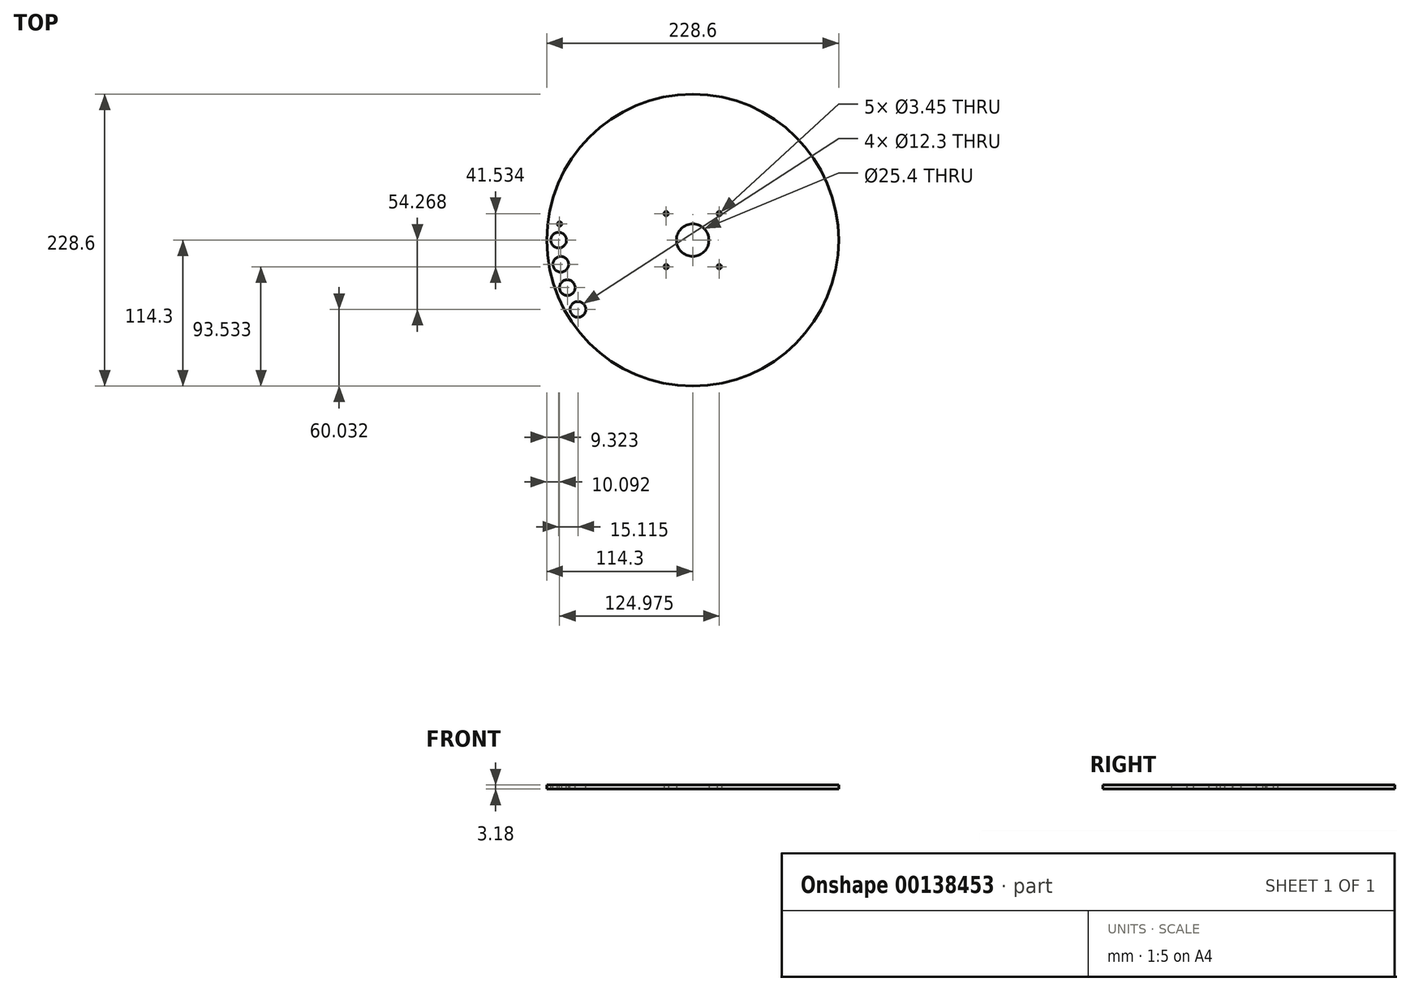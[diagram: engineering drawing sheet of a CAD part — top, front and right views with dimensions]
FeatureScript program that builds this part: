
annotation { "Feature Type Name" : "Feature", "Feature Type Description" : "" }
export const myFeature = defineFeature(function(context is Context, id is Id, definition is map)
    precondition{}
    {
        {
            var Q0;
            Q0=qCreatedBy(makeId("Top.planeOp"),FACE);
            var sketch = newSketch(context, id + "F0", { "sketchPlane" : qUnion([Q0])});
            skCircle(sketch, "E0", {"center": v(0, 0) * mm, "radius": 114.3 * mm});
            skCircle(sketch, "E1", {"center": v(0, 0) * mm, "radius": 12.7 * mm});
            skCircle(sketch, "E2", {"center": v(0, 0) * mm, "radius": 25.4 * mm, "construction": true});
            skLineSegment(sketch, "E3.bottom", {"start": v(-20.77, -20.77) * mm, "end": v(20.77, -20.77) * mm, "construction": true});
            skLineSegment(sketch, "E3.top", {"start": v(-20.77, 20.77) * mm, "end": v(20.77, 20.77) * mm, "construction": true});
            skLineSegment(sketch, "E3.left", {"start": v(-20.77, -20.77) * mm, "end": v(-20.77, 20.77) * mm, "construction": true});
            skLineSegment(sketch, "E3.right", {"start": v(20.77, -20.77) * mm, "end": v(20.77, 20.77) * mm, "construction": true});
            skCircle(sketch, "E4", {"center": v(-20.77, -20.77) * mm, "radius": 3.97 * mm, "construction": true});
            skCircle(sketch, "E5", {"center": v(-20.77, -20.77) * mm, "radius": 1.73 * mm});
            skCircle(sketch, "E6", {"center": v(-20.77, 20.77) * mm, "radius": 1.73 * mm});
            skCircle(sketch, "E7", {"center": v(20.77, 20.77) * mm, "radius": 1.73 * mm});
            skCircle(sketch, "E8", {"center": v(20.77, -20.77) * mm, "radius": 1.73 * mm});
            skSolve(sketch);
        }
        {
            var Q0;
            Q0 = qSketchRegion(id + "F0", true);
            extrude(context, id + "F1", {"entities" : qUnion([Q0]), "depth" : 3.17 * mm});
        }
        {
            var Q0;
            Q0=makeQuery(id+"F1.opExtrude","CAP_FACE",FACE,{"disambiguationData":[OSD([sQuery(id+"F0.wireOp",EDGE,"E0"),sQuery(id+"F0.wireOp",EDGE,"E1")])],"isStart":false});
            var sketch = newSketch(context, id + "F2", { "sketchPlane" : qUnion([Q0])});
            skLineSegment(sketch, "E9", {"start": v(0, 0) * mm, "end": v(-104.98, 0) * mm, "construction": true});
            skLineSegment(sketch, "E10", {"start": v(-104.98, 0) * mm, "end": v(-114.3, 0) * mm, "construction": true});
            skCircle(sketch, "E11", {"center": v(-104.98, 0) * mm, "radius": 6.15 * mm});
            skLineSegment(sketch, "E12", {"start": v(0, 0) * mm, "end": v(-103.26, -18.9) * mm, "construction": true});
            skLineSegment(sketch, "E13", {"start": v(0, 0) * mm, "end": v(-98.17, -37.2) * mm, "construction": true});
            skLineSegment(sketch, "E14", {"start": v(0, 0) * mm, "end": v(-89.86, -54.27) * mm, "construction": true});
            skLineSegment(sketch, "E15", {"start": v(0, 0) * mm, "end": v(-104.2, 12.68) * mm, "construction": true});
            skCircle(sketch, "E16", {"center": v(-103.26, -18.9) * mm, "radius": 6.15 * mm});
            skCircle(sketch, "E17", {"center": v(-98.17, -37.2) * mm, "radius": 6.15 * mm});
            skCircle(sketch, "E18", {"center": v(-89.86, -54.27) * mm, "radius": 6.15 * mm});
            skLineSegment(sketch, "E19", {"start": v(-104.98, 0) * mm, "end": v(-103.26, -18.9) * mm, "construction": true});
            skLineSegment(sketch, "E20", {"start": v(-98.17, -37.2) * mm, "end": v(-103.26, -18.9) * mm, "construction": true});
            skLineSegment(sketch, "E21", {"start": v(-98.17, -37.2) * mm, "end": v(-89.86, -54.27) * mm, "construction": true});
            skCircle(sketch, "E22", {"center": v(-104.2, 12.68) * mm, "radius": 1.73 * mm});
            skLineSegment(sketch, "E23", {"start": v(-104.2, 12.68) * mm, "end": v(-104.98, 0) * mm, "construction": true});
            skLineSegment(sketch, "E24", {"start": v(0, 0) * mm, "end": v(-82.65, -64.72) * mm, "construction": true});
            skLineSegment(sketch, "E25", {"start": v(-82.65, -64.72) * mm, "end": v(-89.86, -54.27) * mm, "construction": true});
            skCircle(sketch, "E26", {"center": v(-104.2, 12.68) * mm, "radius": 6.35 * mm, "construction": true});
            skCircle(sketch, "E27", {"center": v(-104.98, 0) * mm, "radius": 6.35 * mm, "construction": true});
            skSolve(sketch);
        }
        {
            var Q0;
            Q0 = qSketchRegion(id + "F2", true);
            var Q1;
            Q1=makeQuery(id+"F1.opExtrude","CAP_FACE",FACE,{"disambiguationData":[OSD([sQuery(id+"F0.wireOp",EDGE,"E0"),sQuery(id+"F0.wireOp",EDGE,"E1")])],"isStart":true});
            extrude(context, id + "F3", {"entities" : qUnion([Q0]), "operationType" : NewBodyOperationType.REMOVE, "endBound" : BoundingType.UP_TO_SURFACE, "oppositeDirection" : true, "endBoundEntityFace" : qUnion([Q1]), "depth" : 25.4 * mm});
        }
    });
